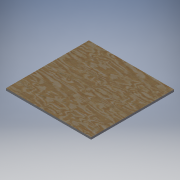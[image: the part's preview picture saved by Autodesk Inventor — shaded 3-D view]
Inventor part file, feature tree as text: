
AUTODESK INVENTOR PART (.ipt)
format: ipt  version: 2018.2 (Build 222227000, 227)  size: 115,712 bytes
history: native  units: in
note: dims shown in document units (in); Inventor stores cm internally (conversion verified against a paired STEP export)
features: extrude x1, sketch x1
ambient origin geometry x8: Origin, YZ Plane, XZ Plane, XY Plane, X Axis, Y Axis, Z Axis, Center Point
bodies: Solid1 (feature_tree)
feature tree (2):
  extrude  "Extrusion1"  Depth=0.75in
  sketch  "Sketch1"  dims[d0=30.0in d1=0.75in d2=30.898in d3=0.0in]
